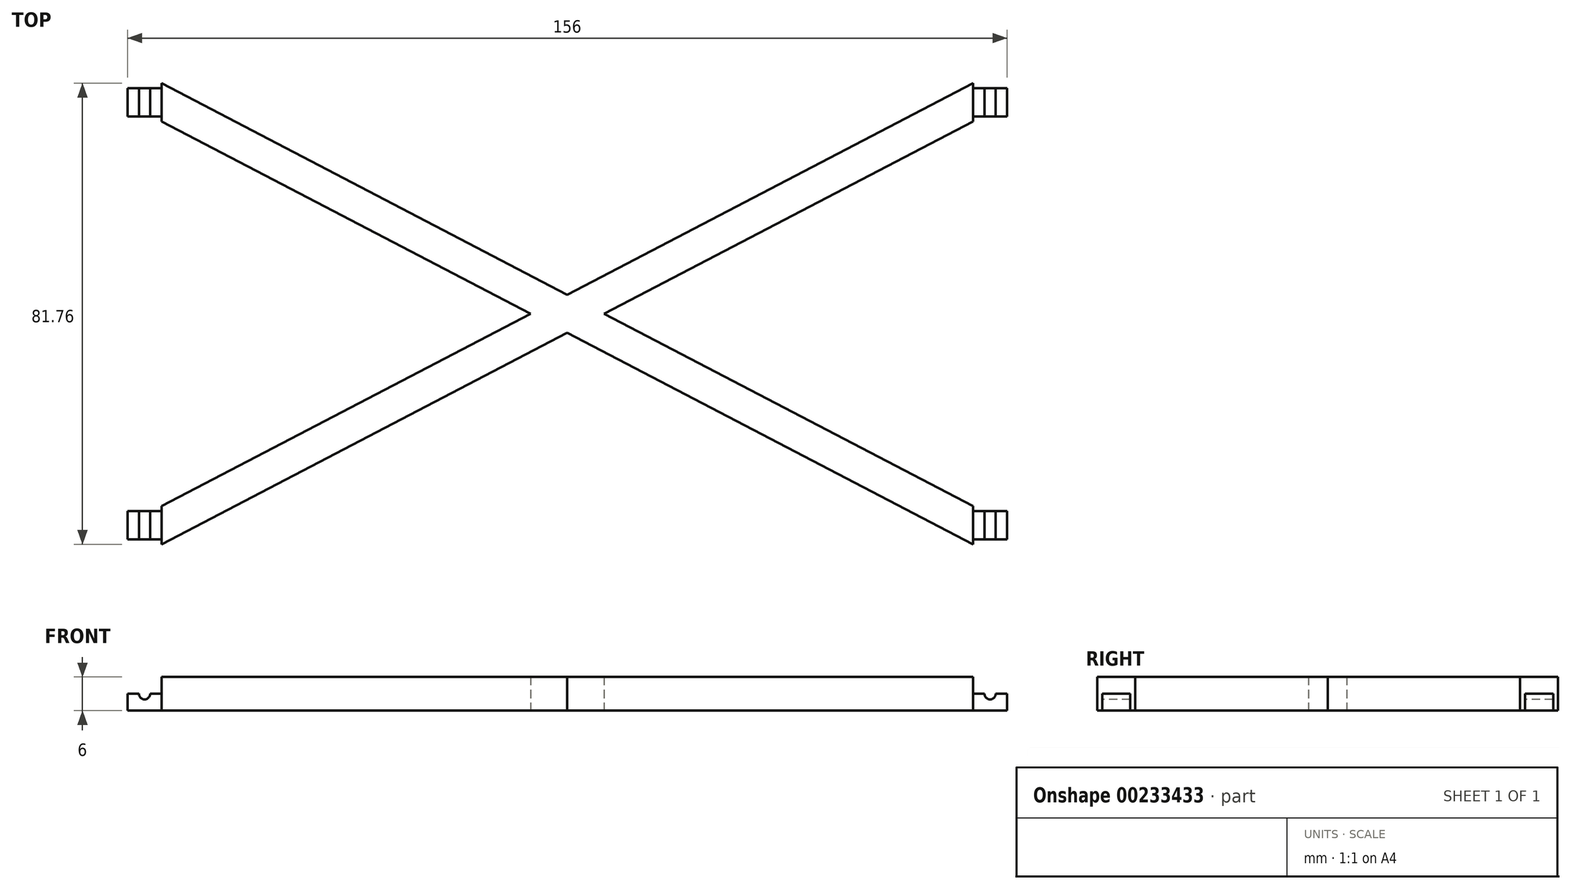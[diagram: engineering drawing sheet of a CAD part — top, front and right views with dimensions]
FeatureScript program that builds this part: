
annotation { "Feature Type Name" : "Feature", "Feature Type Description" : "" }
export const myFeature = defineFeature(function(context is Context, id is Id, definition is map)
    precondition{}
    {
        {
            var Q0;
            Q0=qCreatedBy(makeId("Top.planeOp"),FACE);
            var sketch = newSketch(context, id + "F0", { "sketchPlane" : qUnion([Q0])});
            skLineSegment(sketch, "E0.bottom", {"start": v(-72, -37.5) * mm, "end": v(72, -37.5) * mm, "construction": true});
            skLineSegment(sketch, "E0.top", {"start": v(-72, 37.5) * mm, "end": v(72, 37.5) * mm, "construction": true});
            skLineSegment(sketch, "E0.left", {"start": v(-72, -37.5) * mm, "end": v(-72, 37.5) * mm, "construction": true});
            skLineSegment(sketch, "E0.right", {"start": v(72, -37.5) * mm, "end": v(72, 37.5) * mm, "construction": true});
            skPoint(sketch, "E0.middle", {"position": v(0, 0) * mm});
            skLineSegment(sketch, "E1", {"start": v(-72, 37.5) * mm, "end": v(72, -37.5) * mm, "construction": true});
            skLineSegment(sketch, "E2", {"start": v(-72, -37.5) * mm, "end": v(72, 37.5) * mm, "construction": true});
            skLineSegment(sketch, "E3.0", {"start": v(-72, 40.88) * mm, "end": v(0, 3.38) * mm});
            skLineSegment(sketch, "E4.0", {"start": v(-72, 34.12) * mm, "end": v(-6.5, 0) * mm});
            skLineSegment(sketch, "E5.0", {"start": v(-72, -40.88) * mm, "end": v(0, -3.38) * mm});
            skLineSegment(sketch, "E6.0", {"start": v(-72, -34.12) * mm, "end": v(-6.5, 0) * mm});
            skLineSegment(sketch, "E7", {"start": v(-72, 40.88) * mm, "end": v(-72, 34.12) * mm});
            skLineSegment(sketch, "E8", {"start": v(-72, -34.12) * mm, "end": v(-72, -40.88) * mm});
            skLineSegment(sketch, "E9", {"start": v(72, -34.12) * mm, "end": v(72, -40.88) * mm});
            skLineSegment(sketch, "E10", {"start": v(72, 40.88) * mm, "end": v(72, 34.12) * mm});
            skLineSegment(sketch, "E11.trimOffspring", {"start": v(0, 3.38) * mm, "end": v(72, 40.88) * mm});
            skLineSegment(sketch, "E12.trimOffspring", {"start": v(6.5, 0) * mm, "end": v(72, -34.12) * mm});
            skLineSegment(sketch, "E13.trimOffspring", {"start": v(6.5, 0) * mm, "end": v(72, 34.12) * mm});
            skLineSegment(sketch, "E14.trimOffspring", {"start": v(0, -3.38) * mm, "end": v(72, -40.88) * mm});
            skSolve(sketch);
        }
        {
            var Q0;
            Q0 = qSketchRegion(id + "F0", true);
            extrude(context, id + "F1", {"entities" : qUnion([Q0]), "depth" : 6 * mm});
        }
        {
            var Q0;
            Q0=qCreatedBy(makeId("Top.planeOp"),FACE);
            var sketch = newSketch(context, id + "F2", { "sketchPlane" : qUnion([Q0])});
            skLineSegment(sketch, "E15.bottom", {"start": v(-78, 40) * mm, "end": v(-72, 40) * mm});
            skLineSegment(sketch, "E15.top", {"start": v(-78, 35) * mm, "end": v(-72, 35) * mm});
            skLineSegment(sketch, "E15.left", {"start": v(-78, 40) * mm, "end": v(-78, 35) * mm});
            skLineSegment(sketch, "E15.right", {"start": v(-72, 40) * mm, "end": v(-72, 35) * mm});
            skLineSegment(sketch, "E16.bottom", {"start": v(-78, -35) * mm, "end": v(-72, -35) * mm});
            skLineSegment(sketch, "E16.top", {"start": v(-78, -40) * mm, "end": v(-72, -40) * mm});
            skLineSegment(sketch, "E16.left", {"start": v(-78, -35) * mm, "end": v(-78, -40) * mm});
            skLineSegment(sketch, "E16.right", {"start": v(-72, -35) * mm, "end": v(-72, -40) * mm});
            skLineSegment(sketch, "E17.bottom", {"start": v(72, -35) * mm, "end": v(78, -35) * mm});
            skLineSegment(sketch, "E17.top", {"start": v(72, -40) * mm, "end": v(78, -40) * mm});
            skLineSegment(sketch, "E17.left", {"start": v(72, -35) * mm, "end": v(72, -40) * mm});
            skLineSegment(sketch, "E17.right", {"start": v(78, -35) * mm, "end": v(78, -40) * mm});
            skLineSegment(sketch, "E18.bottom", {"start": v(72, 40) * mm, "end": v(78, 40) * mm});
            skLineSegment(sketch, "E18.top", {"start": v(72, 35) * mm, "end": v(78, 35) * mm});
            skLineSegment(sketch, "E18.left", {"start": v(72, 40) * mm, "end": v(72, 35) * mm});
            skLineSegment(sketch, "E18.right", {"start": v(78, 40) * mm, "end": v(78, 35) * mm});
            skSolve(sketch);
        }
        {
            var Q0;
            Q0=makeQuery(id+"F2.imprint","IMPRINT",FACE,{"disambiguationData":[TD([[makeQuery(id+"F2.imprint","IMPRINT",EDGE,{"derivedFrom":sQuery(id+"F2.wireOp",EDGE,"E15.bottom")}),-1.0]])]});
            var Q1;
            Q1=makeQuery(id+"F2.imprint","IMPRINT",FACE,{"disambiguationData":[TD([[makeQuery(id+"F2.imprint","IMPRINT",EDGE,{"derivedFrom":sQuery(id+"F2.wireOp",EDGE,"E16.bottom")}),-1.0]])]});
            var Q2;
            Q2=makeQuery(id+"F2.imprint","IMPRINT",FACE,{"disambiguationData":[TD([[makeQuery(id+"F2.imprint","IMPRINT",EDGE,{"derivedFrom":sQuery(id+"F2.wireOp",EDGE,"E17.bottom")}),-1.0]])]});
            var Q3;
            Q3=makeQuery(id+"F2.imprint","IMPRINT",FACE,{"disambiguationData":[TD([[makeQuery(id+"F2.imprint","IMPRINT",EDGE,{"derivedFrom":sQuery(id+"F2.wireOp",EDGE,"E18.bottom")}),-1.0]])]});
            extrude(context, id + "F3", {"entities" : qUnion([Q0, Q1, Q2, Q3]), "operationType" : NewBodyOperationType.ADD, "depth" : 3 * mm});
        }
        {
            var Q0;
            Q0=makeQuery(id+"F3.opExtrude","SWEPT_FACE",FACE,{"disambiguationData":[OSD([sQuery(id+"F2.wireOp",EDGE,"E16.top")])]});
            var sketch = newSketch(context, id + "F4", { "sketchPlane" : qUnion([Q0])});
            skCircle(sketch, "E19", {"center": v(-75, 3) * mm, "radius": 1 * mm});
            skCircle(sketch, "E20", {"center": v(75, 3) * mm, "radius": 1 * mm});
            skSolve(sketch);
        }
        {
            var Q0;
            {var subQ0=sQuery(id+"F4.wireOp",EDGE,"E19");var subQ1=makeQuery(id+"F3.opExtrude","CAP_EDGE",EDGE,{"disambiguationData":[OSD([sQuery(id+"F2.wireOp",EDGE,"E16.top")])],"isStart":false});var subQ2=makeQuery(id+"F4.imprint","INTERSECT",VERTEX,{"disambiguationData":[OD(0.0)],"derivedFrom":[subQ1,subQ0]});Q0=makeQuery(id+"F4.imprint","IMPRINT",FACE,{"disambiguationData":[TD([[makeQuery(id+"F4.imprint","IMPRINT",EDGE,{"disambiguationData":[TD([[subQ2,-1.0]])],"derivedFrom":subQ0}),1.0]])]});}
            var Q1;
            Q1=makeQuery(id+"F4.imprint","IMPRINT",FACE,{"disambiguationData":[TD([[makeQuery(id+"F4.imprint","IMPRINT",EDGE,{"derivedFrom":sQuery(id+"F4.wireOp",EDGE,"E20")}),1.0]])]});
            extrude(context, id + "F5", {"entities" : qUnion([Q0, Q1]), "operationType" : NewBodyOperationType.REMOVE, "oppositeDirection" : true, "depth" : 100 * mm});
        }
    });
